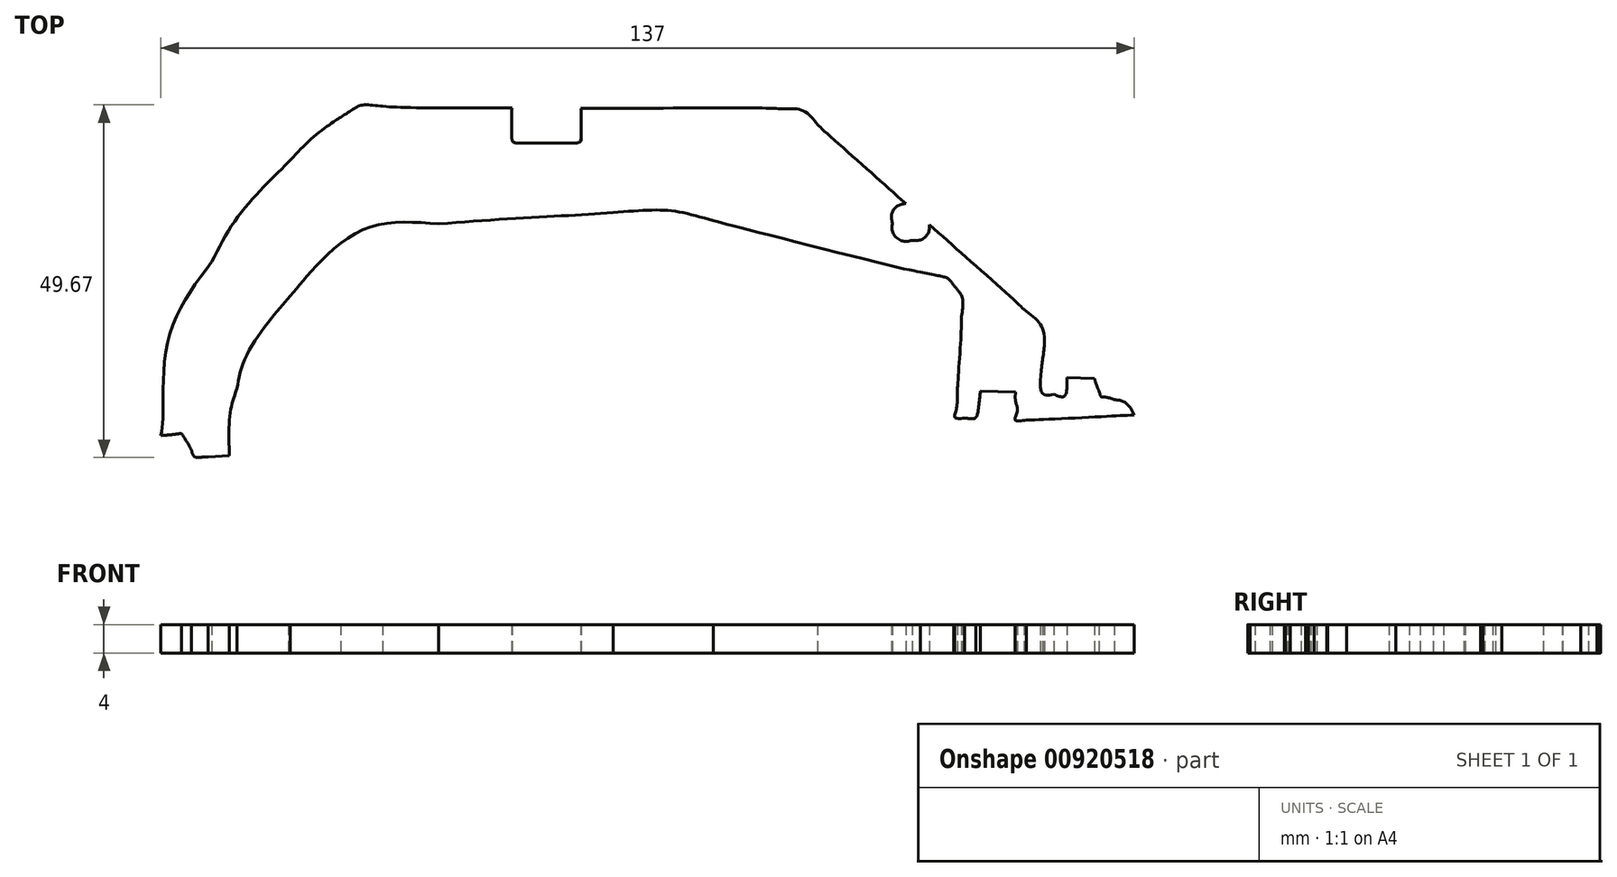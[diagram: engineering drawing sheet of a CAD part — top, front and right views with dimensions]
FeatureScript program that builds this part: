
annotation { "Feature Type Name" : "Feature", "Feature Type Description" : "" }
export const myFeature = defineFeature(function(context is Context, id is Id, definition is map)
    precondition{}
    {
        {
            var Q0;
            Q0=qCreatedBy(makeId("Top.planeOp"),FACE);
            var sketch = newSketch(context, id + "F0", { "sketchPlane" : qUnion([Q0])});
            skFitSpline(sketch, "E0", {"points": [v(66.2, -16.42) * mm, v(64.66, -16.03) * mm, v(64.38, -16.06) * mm, v(64.04, -15.24) * mm]});
            skFitSpline(sketch, "E1", {"points": [v(64.04, -15.24) * mm, v(63.7, -14.44) * mm, v(63.4, -13.46) * mm, v(63.4, -13.45) * mm, v(63.4, -13.45) * mm, v(63.4, -13.45) * mm]});
            skFitSpline(sketch, "E2", {"points": [v(63.4, -13.45) * mm, v(63.4, -13.45) * mm, v(63.4, -13.45) * mm, v(63.37, -13.45) * mm, v(59.55, -13.3) * mm, v(59.53, -13.3) * mm, v(59.53, -13.3) * mm, v(59.53, -13.3) * mm]});
            skFitSpline(sketch, "E3", {"points": [v(59.53, -13.3) * mm, v(59.53, -13.3) * mm, v(59.53, -13.3) * mm, v(59.53, -13.32) * mm, v(59.27, -15.78) * mm, v(57.67, -15.66) * mm]});
            skFitSpline(sketch, "E4", {"points": [v(57.67, -15.66) * mm, v(56.07, -15.53) * mm, v(55.87, -12.67) * mm, v(56.1, -10.64) * mm]});
            skFitSpline(sketch, "E5", {"points": [v(56.1, -10.64) * mm, v(56.34, -8.6) * mm, v(55.88, -6.04) * mm, v(53.46, -3.72) * mm]});
            skFitSpline(sketch, "E6", {"points": [v(53.46, -3.72) * mm, v(52.34, -2.63) * mm, v(46.4, 2.66) * mm, v(40.17, 8.2) * mm]});
            skFitSpline(sketch, "E7", {"points": [v(40.17, 8.2) * mm, v(39.97, 7.03) * mm, v(38.98, 6.1) * mm, v(37.74, 6.02) * mm]});
            skFitSpline(sketch, "E8", {"points": [v(37.74, 6.02) * mm, v(36.28, 5.93) * mm, v(35.03, 7.03) * mm, v(34.93, 8.5) * mm]});
            skFitSpline(sketch, "E9", {"points": [v(34.93, 8.5) * mm, v(34.85, 9.75) * mm, v(35.66, 10.85) * mm, v(36.82, 11.2) * mm]});
            skFitSpline(sketch, "E10", {"points": [v(36.82, 11.2) * mm, v(30.84, 16.52) * mm, v(25.35, 21.42) * mm, v(24.42, 22.3) * mm]});
            skFitSpline(sketch, "E11", {"points": [v(24.42, 22.3) * mm, v(22.36, 24.26) * mm, v(19.71, 24.56) * mm, v(17.73, 24.6) * mm]});
            skFitSpline(sketch, "E12", {"points": [v(17.73, 24.6) * mm, v(14.65, 24.66) * mm, v(2.97, 24.63) * mm, v(-8.9, 24.63) * mm]});
            skFitSpline(sketch, "E13", {"points": [v(-8.9, 24.63) * mm, v(-8.87, 24.52) * mm, v(-8.85, 24.41) * mm, v(-8.85, 24.3) * mm, v(-8.85, 24.3) * mm, v(-8.85, 24.29) * mm, v(-8.87, 20.7) * mm, v(-8.87, 20.7) * mm, v(-8.87, 20.7) * mm, v(-8.87, 20.14) * mm, v(-9.32, 19.7) * mm, v(-9.87, 19.7) * mm, v(-9.87, 19.7) * mm, v(-9.87, 19.7) * mm, v(-17.67, 19.74) * mm, v(-17.67, 19.74) * mm, v(-17.67, 19.74) * mm, v(-18.22, 19.74) * mm, v(-18.66, 20.2) * mm, v(-18.66, 20.74) * mm, v(-18.66, 20.74) * mm, v(-18.66, 20.74) * mm, v(-18.64, 24.34) * mm, v(-18.64, 24.34) * mm, v(-18.64, 24.34) * mm, v(-18.64, 24.45) * mm, v(-18.62, 24.55) * mm, v(-18.59, 24.64) * mm]});
            skFitSpline(sketch, "E14", {"points": [v(-18.59, 24.64) * mm, v(-26.91, 24.67) * mm, v(-34.1, 24.73) * mm, v(-36.78, 24.89) * mm]});
            skFitSpline(sketch, "E15", {"points": [v(-36.78, 24.89) * mm, v(-39.65, 25.05) * mm, v(-40.76, 24.6) * mm, v(-42.7, 23.36) * mm]});
            skFitSpline(sketch, "E16", {"points": [v(-42.7, 23.36) * mm, v(-43.67, 22.74) * mm, v(-46.6, 20.52) * mm, v(-50.08, 17.02) * mm]});
            skFitSpline(sketch, "E17", {"points": [v(-50.08, 17.02) * mm, v(-53.57, 13.52) * mm, v(-57.63, 8.74) * mm, v(-60.87, 3) * mm]});
            skFitSpline(sketch, "E18", {"points": [v(-60.87, 3) * mm, v(-66.93, -7.71) * mm, v(-67.75, -18.44) * mm, v(-68.03, -21.47) * mm]});
            skFitSpline(sketch, "E19", {"points": [v(-68.03, -21.47) * mm, v(-66.51, -21.34) * mm, v(-65.15, -21.18) * mm, v(-65.13, -21.17) * mm, v(-65.13, -21.17) * mm, v(-65.13, -21.17) * mm]});
            skFitSpline(sketch, "E20", {"points": [v(-65.13, -21.17) * mm, v(-65.13, -21.17) * mm, v(-65.13, -21.17) * mm, v(-65.12, -21.2) * mm, v(-64.24, -22.58) * mm, v(-63.74, -23.53) * mm]});
            skFitSpline(sketch, "E21", {"points": [v(-63.74, -23.53) * mm, v(-63.24, -24.5) * mm, v(-62.44, -24.54) * mm, v(-61.39, -24.47) * mm]});
            skFitSpline(sketch, "E22", {"points": [v(-61.39, -24.47) * mm, v(-60.34, -24.4) * mm, v(-58.4, -24.28) * mm, v(-58.4, -24.28) * mm, v(-58.4, -24.28) * mm, v(-58.4, -24.28) * mm]});
            skFitSpline(sketch, "E23", {"points": [v(-58.4, -24.28) * mm, v(-58.4, -24.28) * mm, v(-58.4, -24.28) * mm, v(-58.4, -24.24) * mm, v(-58.36, -18.96) * mm, v(-57.3, -14.85) * mm]});
            skFitSpline(sketch, "E24", {"points": [v(-57.3, -14.85) * mm, v(-56.24, -10.71) * mm, v(-52.53, -5) * mm, v(-49.82, -1.82) * mm]});
            skFitSpline(sketch, "E25", {"points": [v(-49.82, -1.82) * mm, v(-47.1, 1.35) * mm, v(-39.47, 7.56) * mm, v(-28.92, 8.32) * mm]});
            skFitSpline(sketch, "E26", {"points": [v(-28.92, 8.32) * mm, v(-18.37, 9.09) * mm, v(-10.2, 9.54) * mm, v(-4.38, 9.91) * mm]});
            skFitSpline(sketch, "E27", {"points": [v(-4.38, 9.91) * mm, v(1.42, 10.28) * mm, v(5.06, 9.99) * mm, v(9.73, 8.78) * mm]});
            skFitSpline(sketch, "E28", {"points": [v(9.73, 8.78) * mm, v(14.4, 7.58) * mm, v(35.94, 2.16) * mm, v(38.9, 1.56) * mm]});
            skFitSpline(sketch, "E29", {"points": [v(38.9, 1.56) * mm, v(41.85, 0.95) * mm, v(42.8, 0.6) * mm, v(43.57, -0.32) * mm]});
            skFitSpline(sketch, "E30", {"points": [v(43.57, -0.32) * mm, v(44.1, -0.95) * mm, v(44.76, -2.05) * mm, v(44.68, -4.7) * mm]});
            skFitSpline(sketch, "E31", {"points": [v(44.68, -4.7) * mm, v(44.62, -6.94) * mm, v(44.2, -13.56) * mm, v(44.06, -15.69) * mm]});
            skFitSpline(sketch, "E32", {"points": [v(44.06, -15.69) * mm, v(43.93, -17.82) * mm, v(43.75, -18.93) * mm, v(45.08, -19.02) * mm]});
            skFitSpline(sketch, "E33", {"points": [v(45.08, -19.02) * mm, v(46.41, -19.1) * mm, v(46.52, -19.08) * mm, v(46.68, -18.9) * mm]});
            skFitSpline(sketch, "E34", {"points": [v(46.68, -18.9) * mm, v(46.85, -18.7) * mm, v(47.33, -15.23) * mm, v(47.34, -15.2) * mm, v(47.34, -15.2) * mm, v(47.34, -15.2) * mm]});
            skFitSpline(sketch, "E35", {"points": [v(47.34, -15.2) * mm, v(47.34, -15.2) * mm, v(47.34, -15.2) * mm, v(47.37, -15.2) * mm, v(52.24, -15.33) * mm, v(52.27, -15.34) * mm, v(52.27, -15.34) * mm, v(52.27, -15.34) * mm]});
            skFitSpline(sketch, "E36", {"points": [v(52.27, -15.34) * mm, v(52.27, -15.34) * mm, v(52.27, -15.34) * mm, v(52.27, -15.35) * mm, v(52.23, -16.14) * mm, v(52.38, -17.1) * mm]});
            skFitSpline(sketch, "E37", {"points": [v(52.38, -17.1) * mm, v(52.54, -18.06) * mm, v(52.2, -19.28) * mm, v(53.8, -19.27) * mm]});
            skFitSpline(sketch, "E38", {"points": [v(53.8, -19.27) * mm, v(55.02, -19.26) * mm, v(64.62, -18.79) * mm, v(68.97, -18.57) * mm]});
            skFitSpline(sketch, "E39", {"points": [v(68.97, -18.57) * mm, v(68.57, -17.78) * mm, v(67.62, -16.77) * mm, v(66.2, -16.42) * mm]});
            skSolve(sketch);
        }
        {
            var Q0;
            Q0 = qSketchRegion(id + "F0", true);
            extrude(context, id + "F1", {"entities" : qUnion([Q0]), "depth" : 4 * mm, "offsetDistance" : 25 * mm});
        }
    });
